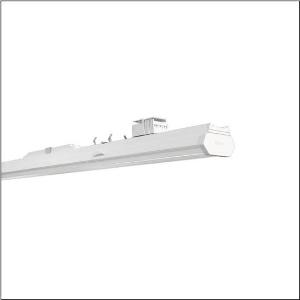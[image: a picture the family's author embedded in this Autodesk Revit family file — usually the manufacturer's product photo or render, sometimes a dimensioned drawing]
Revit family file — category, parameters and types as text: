
# Revit family: licross_r__21_protected_mo_52td12dn48xg_f2a3
name_source: partatom
category: Lighting Fixtures
units: mm (PartAtom-declared; Revit-internal decimal feet)

## family parameters
Cut with Voids When Loaded = No
Host = Face
Light Source = No
Part Type = Normal
Room Calculation Point = No
Round Connector Dimension = Use Diameter
Shared = No

## types (1)
- --- (1 x LED, 8000 lm, 45.3 W, 4000K)
    Apparent Load = 45 VA
    CIE Flux Codes = 73 92 98 99 100
    Color Rendering = 80
    Color Temperature = 4000K
    Default Elevation = 1800 mm
    Description = Licross® 21 Protected MO, luminaire insert, of sheet steel, galvanised, coil coated, white, length: 1.500mm, width: 90mm, height: 103mm, LED rated luminous flux: 8.000lm, light colour: 840, control gear: DALI 2, with plug, 5-pole, with phase selection, mains connection: 220..240V, AC, 50/60Hz, rated input power: 45W, halogen-free wiring, primary light control with lens, of plastic, primary optical cover: cover, of PMMA, light emission: direct distribution, primary light characteristic: symmetric, protection rating (complete): IP54, insulation class (complete): insulation class I (protective earthing), certification: CE, ENEC, VDE, UKCA, protection symbol: D if used in an environment with non-conductive dust loads with corresponding accessories, impact resistance: IK06, permissible ambient temperature for indoor applications: -25..+45°C, corresponds to IFS (International Featured Standards) requirements for safety and quality in the food industry, reducing of maximum allowable ambient temperature of 5°C with ceiling mounting, LABS conformity tested according to VDMA 24364:2018-05, packaging unit: 1 piece
    Height = 92 mm
    Lamp = 1 x LED
    Lamp Light Flux = 8000 lm
    Lamp Power = 45.3 W
    Lamp count = 1
    Length = 1500 mm
    Luminous efficacy = 177 lm/W
    Manufacturer = Siteco
    ModVariant = No
    Model = 52TD12DN48XG
    Mounting Place = Ceiling
    Mounting Type = Pendant
    Number of Poles = 1
    OnlyDefault = Yes
    Power Factor = 1
    Product Name = Licross® 21 Protected MO
    Product group = luminaire insert
    ProductGroupID = 901
    Protection Class = Protection class I
    Protection Degree = IP 54
    RLX_Detail_Level = 1
    RLX_Emergency_Light_Flux = 0 lm
    RLX_Emergency_Type = 0
    RLX_Emergency_Type_DB = No
    RlxData = <blob elided: 24437 chars, md5=c18517dd>
    Socket = socket
    Standby Power = 0 W
    System Light Flux = 8000 lm
    System Power = 45 W
    Type Comments = factory setting: luminous flux: 100 % | dim-lin: 254 | 305 mA
    Type Image = l_1256148.jpg
    URL = http://relux.com
    VarID = @adj_078413
    Voltage = 0 V
    Weight = 0.00 kg
    Width = 88 mm

## geometry (parser evidence)
native form markers: Blend x4, Sweep x10
no freeform markers — native parametric forms only
